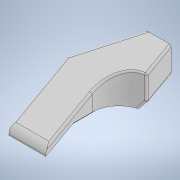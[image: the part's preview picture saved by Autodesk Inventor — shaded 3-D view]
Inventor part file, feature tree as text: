
AUTODESK INVENTOR PART (.ipt)
format: ipt  version: 2020 (Build 240168000, 168)  size: 354,816 bytes
history: native  units: mm
features: extrude x18, sketch x18, fillet x7, plane x3, projected_geometry x3, other x2, loft x1
ambient origin geometry x8: Origin, YZ Plane, XZ Plane, XY Plane, X Axis, Y Axis, Z Axis, Center Point
bodies: Solid1 (feature_tree)
feature tree (52):
  extrude  "Extrusion1"  Depth=5.2mm
  sketch  "Sketch2"  dims[d2=3.125mm d3=3.0mm]
  extrude  "Extrusion2"  Depth=3.0mm
  extrude  "Extrusion3"  Depth=3.0mm
  extrude  "Extrusion4"  Depth=0.65mm
  loft  "Loft1"
  plane  "Work Plane1"
  extrude  "Extrusion5"  Depth=5.0mm
  fillet  "Fillet2"  Radius=15.0mm
  extrude  "Extrusion6"  Depth=22.0mm
  fillet  "Fillet3"  Radius=12.0mm
  extrude  "Extrusion7"  Depth=26.2mm TaperAngle=0.0deg
  extrude  "Extrusion8"  Depth=10.0mm TaperAngle=0.0deg
  sketch  "Sketch8"  dims[d17=11.0mm d18=0.0mm d19=26.2mm d20=0.0mm]
  extrude  "Extrusion9"  TaperAngle=0.0deg  [1 undecoded]
  extrude  "Extrusion10"  Depth=2.0mm TaperAngle=0.0deg
  fillet  "Fillet4"  Radius=2.0mm
  fillet  "Fillet5"  Radius=10.25mm
  plane  "Work Plane2"
  plane  "Work Plane3"
  extrude  "Extrusion11"  Depth=2.0mm TaperAngle=0.0deg
  extrude  "Extrusion12"  Depth=2.0mm TaperAngle=0.0deg
  fillet  "Fillet6"  Radius=100.0mm
  extrude  "Extrusion13"  Depth=2.0mm
  fillet  "Fillet7"  [1 undecoded]
  extrude  "Extrusion14"  TaperAngle=90.0deg  [1 undecoded]
  extrude  "Extrusion15"  Depth=2.0mm
  extrude  "Extrusion16"  Depth=2.0mm
  extrude  "Extrusion17"  Depth=2.0mm TaperAngle=0.0deg
  fillet  "Fillet8"  Radius=2.0mm
  extrude  "Extrusion18"  Depth=2.0mm TaperAngle=0.0deg
  sketch  "Sketch1"  dims[d0=15.75mm d1=5.2mm]
  sketch  "Sketch3"  dims[d4=3.125mm d5=3.0mm]
  other  "Edges1"
  other  "Edges2"
  sketch  "Sketch4"  dims[d6=0.65mm d7=0.65mm]
  sketch  "Sketch5"  dims[d8=2.25mm d9=2.25mm]
  sketch  "Sketch6"  dims[d10=60.0mm d11=0.0mm d12=5.0mm d13=15.0mm]
  sketch  "Sketch7"  dims[d14=47.0mm d15=22.0mm d16=12.0mm]
  sketch  "Sketch9"  dims[d22=10.0mm d23=38.0mm d24=0.0mm]
  projected_geometry  "Projected Loop1"
  sketch  "Sketch10"  dims[d25=0.0mm d26=90.0deg d27=0.0mm d28=90.0deg]
  sketch  "Sketch11"  dims[d29=-7.853982mm d30=27.55mm d31=0.0mm d33=2.0mm d34=10.25mm d35=0.0mm]
  sketch  "Sketch12"  dims[d36=2.0mm d37=6.0mm d38=0.0mm]
  sketch  "Sketch13"  dims[d39=6.0mm d40=0.0mm d41=2.0mm d42=0.0mm d43=100.0mm d44=0.0mm]
  sketch  "Sketch14"  dims[d45=27.0mm d46=2.0mm d47=45.0deg d48=-17.0mm]
  projected_geometry  "Projected Loop2"
  sketch  "Sketch15"  dims[d49=100.0mm d50=0.0mm d51=90.0deg]
  sketch  "Sketch16"  dims[d52=37.2mm d53=0.0mm d54=2.0mm]
  projected_geometry  "Projected Loop3"
  sketch  "Sketch17"  dims[d55=10.0mm d56=0.0mm d57=2.0mm]
  sketch  "Sketch18"  dims[d58=2.0mm d59=0.0mm d60=2.0mm d61=0.0mm d62=2.0mm d63=0.0mm d64=2.0mm d65=0.0mm d66=10.0mm d67=37.2mm d68=0.0mm]
note: 3 required parameter values undecoded (feature->parameter linkage not recoverable at this tier; creation-order binding heuristic only, values carry confidence <= 0.55)
